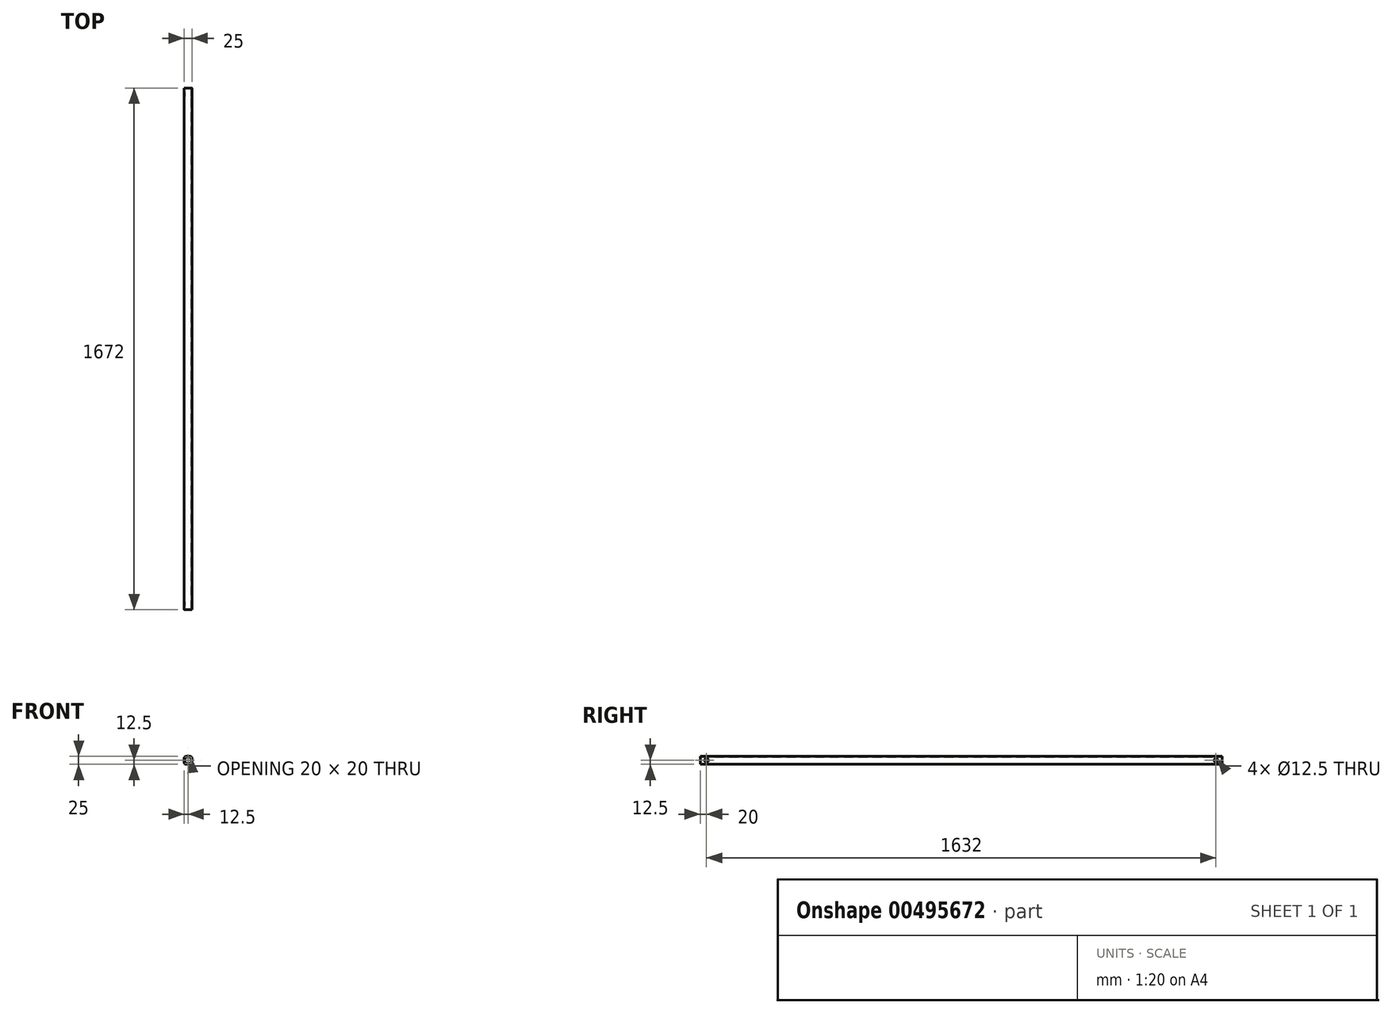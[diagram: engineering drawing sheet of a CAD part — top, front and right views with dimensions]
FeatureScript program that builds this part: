
annotation { "Feature Type Name" : "Feature", "Feature Type Description" : "" }
export const myFeature = defineFeature(function(context is Context, id is Id, definition is map)
    precondition{}
    {
        {
            var Q0;
            Q0=qCreatedBy(makeId("Front.planeOp"),FACE);
            var sketch = newSketch(context, id + "F0", { "sketchPlane" : qUnion([Q0])});
            skLineSegment(sketch, "E0.bottom", {"start": v(7.5, 12.5) * mm, "end": v(-7.5, 12.5) * mm});
            skLineSegment(sketch, "E0.top", {"start": v(7.5, -12.5) * mm, "end": v(-7.5, -12.5) * mm});
            skLineSegment(sketch, "E0.left", {"start": v(12.5, 7.5) * mm, "end": v(12.5, -7.5) * mm});
            skLineSegment(sketch, "E0.right", {"start": v(-12.5, 7.5) * mm, "end": v(-12.5, -7.5) * mm});
            skPoint(sketch, "E0.middle", {"position": v(0, 0) * mm});
            skPoint(sketch, "E1.visualSharp", {"position": v(-12.5, 12.5) * mm});
            skArc(sketch, "E1.filletArc", {"start": v(-7.5, 12.5) * mm, "mid": v(-11.04, 11.04) * mm, "end": v(-12.5, 7.5) * mm});
            skPoint(sketch, "E2.visualSharp", {"position": v(12.5, 12.5) * mm});
            skArc(sketch, "E2.filletArc", {"start": v(12.5, 7.5) * mm, "mid": v(11.04, 11.04) * mm, "end": v(7.5, 12.5) * mm});
            skPoint(sketch, "E3.visualSharp", {"position": v(12.5, -12.5) * mm});
            skArc(sketch, "E3.filletArc", {"start": v(7.5, -12.5) * mm, "mid": v(11.04, -11.04) * mm, "end": v(12.5, -7.5) * mm});
            skPoint(sketch, "E4.visualSharp", {"position": v(-12.5, -12.5) * mm});
            skArc(sketch, "E4.filletArc", {"start": v(-12.5, -7.5) * mm, "mid": v(-11.04, -11.04) * mm, "end": v(-7.5, -12.5) * mm});
            skLineSegment(sketch, "E5.0", {"start": v(7.5, 10) * mm, "end": v(-7.5, 10) * mm});
            skArc(sketch, "E5.1", {"start": v(10, 7.5) * mm, "mid": v(9.27, 9.27) * mm, "end": v(7.5, 10) * mm});
            skArc(sketch, "E5.2", {"start": v(-7.5, 10) * mm, "mid": v(-9.27, 9.27) * mm, "end": v(-10, 7.5) * mm});
            skLineSegment(sketch, "E5.3", {"start": v(10, 7.5) * mm, "end": v(10, -7.5) * mm});
            skLineSegment(sketch, "E5.4", {"start": v(-10, 7.5) * mm, "end": v(-10, -7.5) * mm});
            skArc(sketch, "E5.5", {"start": v(-10, -7.5) * mm, "mid": v(-9.27, -9.27) * mm, "end": v(-7.5, -10) * mm});
            skLineSegment(sketch, "E5.6", {"start": v(7.5, -10) * mm, "end": v(-7.5, -10) * mm});
            skArc(sketch, "E5.7", {"start": v(7.5, -10) * mm, "mid": v(9.27, -9.27) * mm, "end": v(10, -7.5) * mm});
            skSolve(sketch);
        }
        {
            var Q0;
            Q0 = qSketchRegion(id + "F0", true);
            extrude(context, id + "F1", {"entities" : qUnion([Q0]), "endBound" : BoundingType.SYMMETRIC, "depth" : 1672 * mm});
        }
        {
            var Q0;
            Q0=makeQuery(id+"F1.opExtrude","SWEPT_FACE",FACE,{"disambiguationData":[OSD([sQuery(id+"F0.wireOp",EDGE,"E0.left")])]});
            var sketch = newSketch(context, id + "F2", { "sketchPlane" : qUnion([Q0])});
            skLineSegment(sketch, "E6", {"start": v(-836, 0) * mm, "end": v(-816, 0) * mm, "construction": true});
            skCircle(sketch, "E7", {"center": v(-816, 0) * mm, "radius": 6.25 * mm});
            skLineSegment(sketch, "E8", {"start": v(0, 0) * mm, "end": v(0, 13.57) * mm, "construction": true});
            skPoint(sketch, "E8.endSnap0", {"position": v(0, 7.5) * mm});
            skCircle(sketch, "E9.MirrorC", {"center": v(816, 0) * mm, "radius": 6.25 * mm});
            skSolve(sketch);
        }
        {
            var Q0;
            Q0 = qSketchRegion(id + "F2", true);
            extrude(context, id + "F3", {"entities" : qUnion([Q0]), "operationType" : NewBodyOperationType.REMOVE, "endBound" : BoundingType.THROUGH_ALL, "oppositeDirection" : true, "depth" : 25 * mm});
        }
    });
